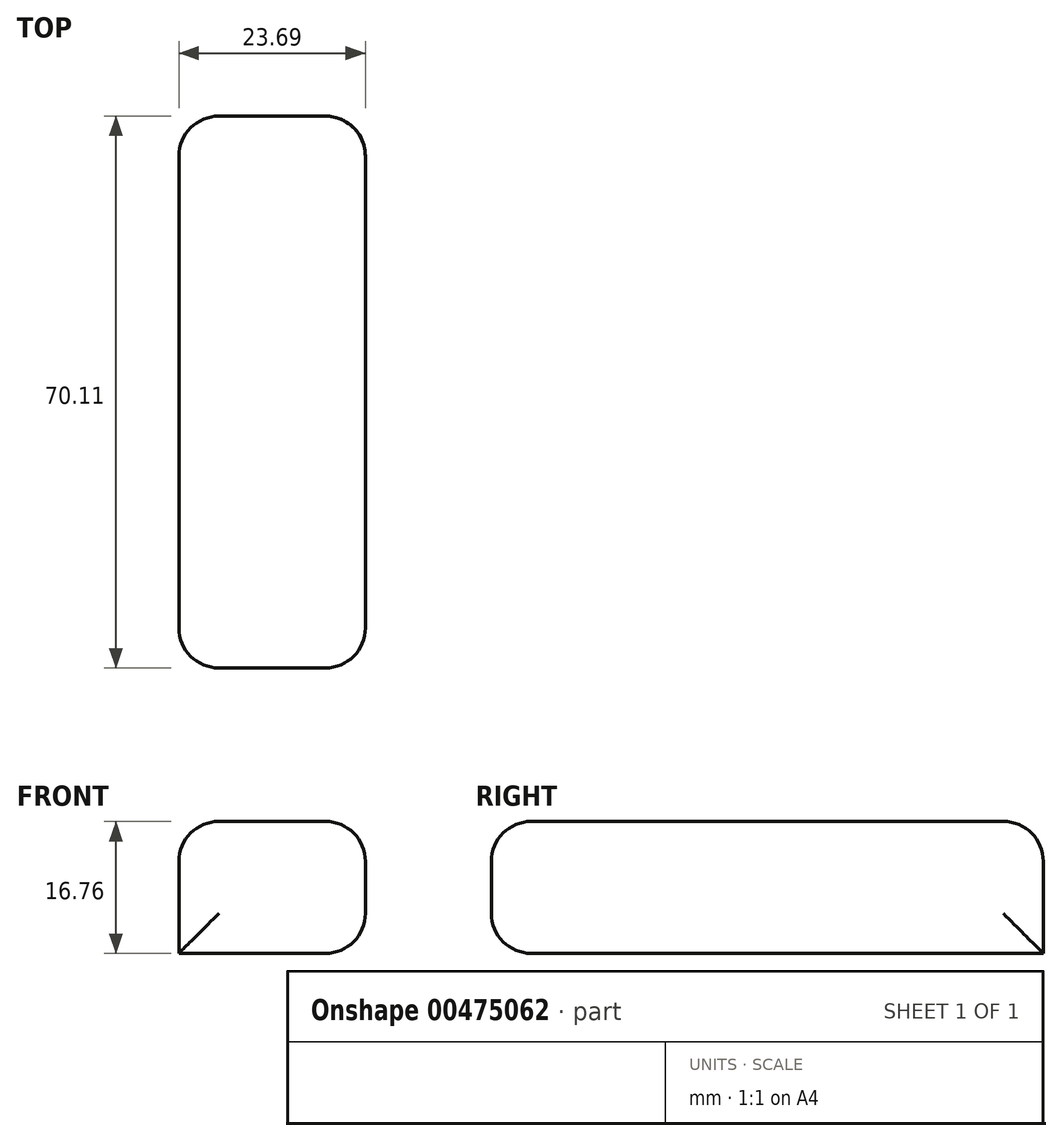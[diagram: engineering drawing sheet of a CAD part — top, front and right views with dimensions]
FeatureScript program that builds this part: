
annotation { "Feature Type Name" : "Feature", "Feature Type Description" : "" }
export const myFeature = defineFeature(function(context is Context, id is Id, definition is map)
    precondition{}
    {
        {
            var Q0;
            Q0=qCreatedBy(makeId("Top.planeOp"),FACE);
            var sketch = newSketch(context, id + "F0", { "sketchPlane" : qUnion([Q0])});
            skLineSegment(sketch, "E0.bottom", {"start": v(-62.56, 28.88) * mm, "end": v(-38.87, 28.88) * mm});
            skLineSegment(sketch, "E0.top", {"start": v(-62.56, -41.23) * mm, "end": v(-38.87, -41.23) * mm});
            skLineSegment(sketch, "E0.left", {"start": v(-62.56, 28.88) * mm, "end": v(-62.56, -41.23) * mm});
            skLineSegment(sketch, "E0.right", {"start": v(-38.87, 28.88) * mm, "end": v(-38.87, -41.23) * mm});
            skSolve(sketch);
        }
        {
            var Q0;
            Q0=makeQuery(id+"F0.imprint","IMPRINT",FACE,{"disambiguationData":[TD([[makeQuery(id+"F0.imprint","IMPRINT",EDGE,{"derivedFrom":sQuery(id+"F0.wireOp",EDGE,"E0.bottom")}),-1.0]])]});
            extrude(context, id + "F1", {"entities" : qUnion([Q0]), "depth" : 16.76 * mm});
        }
        {
            var Q0;
            Q0=makeQuery(id+"F1.opExtrude","CAP_FACE",FACE,{"disambiguationData":[OSD([sQuery(id+"F0.wireOp",EDGE,"E0.bottom"),sQuery(id+"F0.wireOp",EDGE,"E0.top"),sQuery(id+"F0.wireOp",EDGE,"E0.left"),sQuery(id+"F0.wireOp",EDGE,"E0.right")])],"isStart":false});
            var Q1;
            Q1=makeQuery(id+"F1.opExtrude","SWEPT_FACE",FACE,{"disambiguationData":[OSD([sQuery(id+"F0.wireOp",EDGE,"E0.right")])]});
            var Q2;
            Q2=makeQuery(id+"F1.opExtrude","SWEPT_FACE",FACE,{"disambiguationData":[OSD([sQuery(id+"F0.wireOp",EDGE,"E0.top")])]});
            fillet(context, id + "F2", {"entities" : qUnion([Q0, Q1, Q2]), "radius" : 5.08 * mm, "tangentPropagation" : true, "allowEdgeOverflow" : false});
        }
        {
            var Q0;
            Q0=makeQuery(id+"F2.opFillet","BLEND_EDGE",EDGE,{"blendedFrom":[makeQuery(id+"F1.opExtrude","CAP_EDGE",EDGE,{"disambiguationData":[OSD([sQuery(id+"F0.wireOp",EDGE,"E0.bottom")])],"isStart":false}),makeQuery(id+"F1.opExtrude","CAP_EDGE",EDGE,{"disambiguationData":[OSD([sQuery(id+"F0.wireOp",EDGE,"E0.left")])],"isStart":false})],"blendedInto":[]});
            fillet(context, id + "F3", {"entities" : qUnion([Q0]), "radius" : 5.08 * mm, "tangentPropagation" : true, "allowEdgeOverflow" : false});
        }
    });
